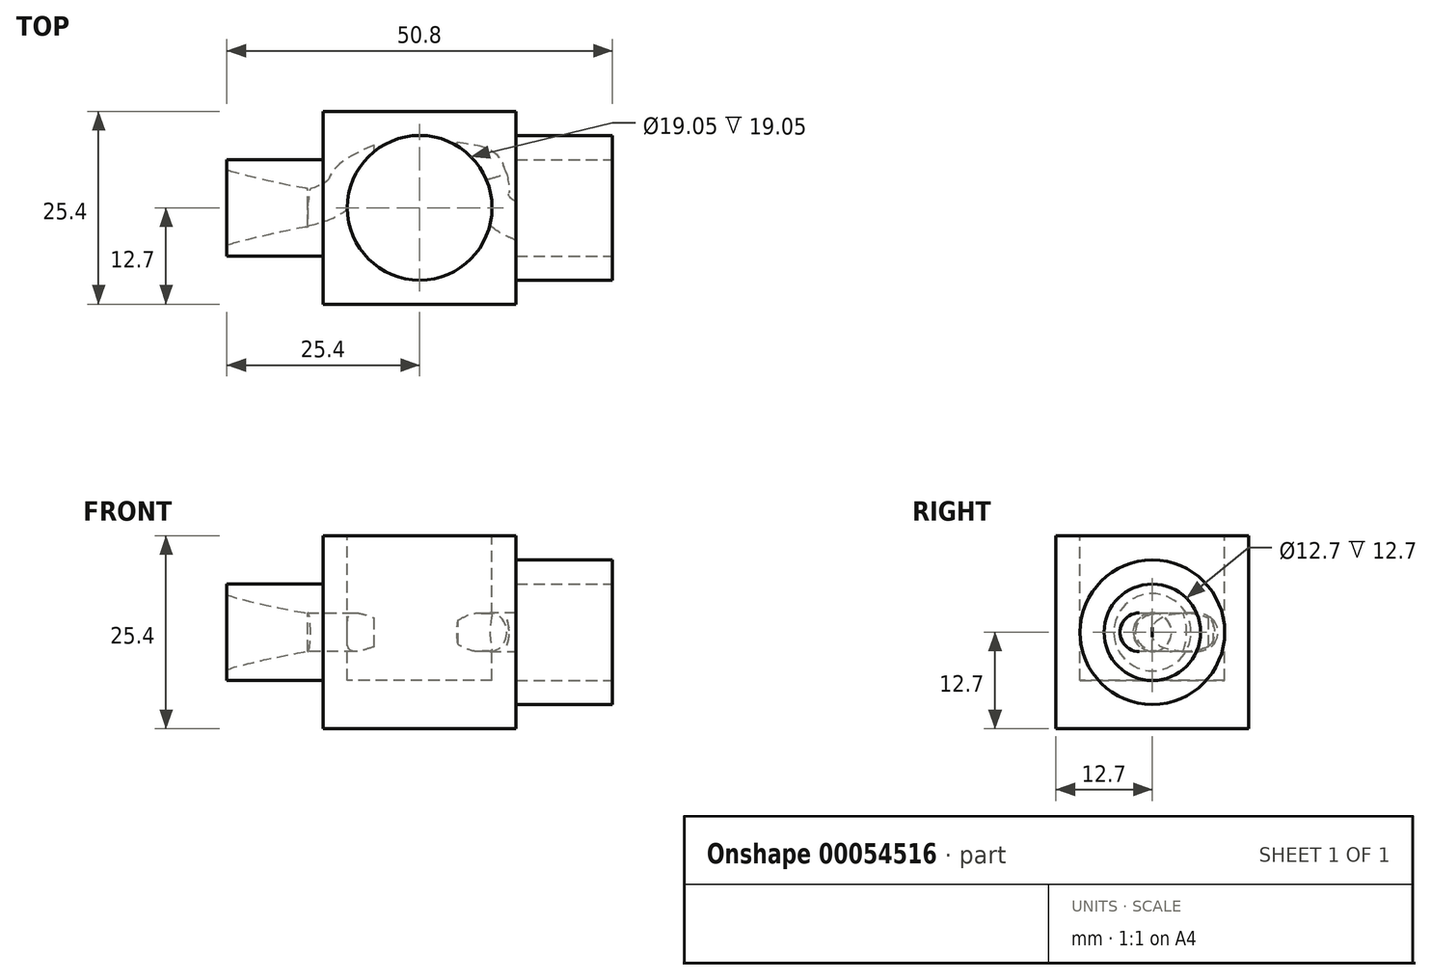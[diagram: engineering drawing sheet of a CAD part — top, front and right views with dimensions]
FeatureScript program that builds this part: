
annotation { "Feature Type Name" : "Feature", "Feature Type Description" : "" }
export const myFeature = defineFeature(function(context is Context, id is Id, definition is map)
    precondition{}
    {
        {
            var Q0;
            Q0=qCreatedBy(makeId("Right.planeOp"),FACE);
            var sketch = newSketch(context, id + "F0", { "sketchPlane" : qUnion([Q0])});
            skCircle(sketch, "E0", {"center": v(0, 0) * mm, "radius": 6.35 * mm});
            skSolve(sketch);
        }
        {
            var Q0;
            Q0=makeQuery(id+"F0.imprint","IMPRINT",FACE,{"disambiguationData":[TD([[makeQuery(id+"F0.imprint","IMPRINT",EDGE,{"derivedFrom":sQuery(id+"F0.wireOp",EDGE,"E0")}),1.0]])]});
            extrude(context, id + "F1", {"entities" : qUnion([Q0]), "depth" : 12.7 * mm});
        }
        {
            var Q0;
            Q0=makeQuery(id+"F1.opExtrude","CAP_FACE",FACE,{"disambiguationData":[OSD([sQuery(id+"F0.wireOp",EDGE,"E0")])],"isStart":false});
            var sketch = newSketch(context, id + "F2", { "sketchPlane" : qUnion([Q0])});
            skLineSegment(sketch, "E1.rect.bottom", {"start": v(12.7, -12.7) * mm, "end": v(-12.7, -12.7) * mm});
            skLineSegment(sketch, "E1.rect.top", {"start": v(12.7, 12.7) * mm, "end": v(-12.7, 12.7) * mm});
            skLineSegment(sketch, "E1.rect.left", {"start": v(12.7, -12.7) * mm, "end": v(12.7, 12.7) * mm});
            skLineSegment(sketch, "E1.rect.right", {"start": v(-12.7, -12.7) * mm, "end": v(-12.7, 12.7) * mm});
            skPoint(sketch, "E1.rect.middle", {"position": v(0, 0) * mm});
            skSolve(sketch);
        }
        {
            var Q0;
            Q0=makeQuery(id+"F2.imprint","IMPRINT",FACE,{"disambiguationData":[TD([[makeQuery(id+"F2.imprint","IMPRINT",EDGE,{"derivedFrom":sQuery(id+"F2.wireOp",EDGE,"E1.rect.bottom")}),-1.0]])]});
            var Q1;
            Q1=makeQuery(id+"F2.imprint","IMPRINT",FACE,{"disambiguationData":[TD([[makeQuery(id+"F2.imprint","IMPRINT",EDGE,{"derivedFrom":makeQuery(id+"F1.opExtrude","CAP_EDGE",EDGE,{"disambiguationData":[OSD([sQuery(id+"F0.wireOp",EDGE,"E0")])],"isStart":false})}),1.0]])]});
            extrude(context, id + "F3", {"entities" : qUnion([Q0, Q1]), "operationType" : NewBodyOperationType.ADD, "depth" : 25.4 * mm});
        }
        {
            var Q0;
            Q0=makeQuery(id+"F3.opExtrude","CAP_FACE",FACE,{"disambiguationData":[OSD([sQuery(id+"F2.wireOp",EDGE,"E1.rect.bottom"),sQuery(id+"F2.wireOp",EDGE,"E1.rect.top"),sQuery(id+"F2.wireOp",EDGE,"E1.rect.left"),sQuery(id+"F2.wireOp",EDGE,"E1.rect.right")])],"isStart":false});
            var sketch = newSketch(context, id + "F4", { "sketchPlane" : qUnion([Q0])});
            skCircle(sketch, "E2", {"center": v(0, 0) * mm, "radius": 9.53 * mm});
            skSolve(sketch);
        }
        {
            var Q0;
            Q0=makeQuery(id+"F4.imprint","IMPRINT",FACE,{"disambiguationData":[TD([[makeQuery(id+"F4.imprint","IMPRINT",EDGE,{"derivedFrom":sQuery(id+"F4.wireOp",EDGE,"E2")}),1.0]])]});
            extrude(context, id + "F5", {"entities" : qUnion([Q0]), "operationType" : NewBodyOperationType.ADD, "depth" : 12.7 * mm});
        }
        {
            var Q0;
            Q0=makeQuery(id+"F3.opExtrude","SWEPT_FACE",FACE,{"disambiguationData":[OSD([sQuery(id+"F2.wireOp",EDGE,"E1.rect.top")])]});
            var sketch = newSketch(context, id + "F6", { "sketchPlane" : qUnion([Q0])});
            skCircle(sketch, "E3", {"center": v(25.4, 0) * mm, "radius": 9.53 * mm});
            skPoint(sketch, "E3.centerSnap0", {"position": v(25.4, 12.7) * mm});
            skSolve(sketch);
        }
        {
            var Q0;
            Q0=makeQuery(id+"F6.imprint","IMPRINT",FACE,{"disambiguationData":[TD([[makeQuery(id+"F6.imprint","IMPRINT",EDGE,{"derivedFrom":sQuery(id+"F6.wireOp",EDGE,"E3")}),1.0]])]});
            extrude(context, id + "F7", {"entities" : qUnion([Q0]), "operationType" : NewBodyOperationType.REMOVE, "oppositeDirection" : true, "depth" : 19.05 * mm});
        }
        {
            var Q0;
            Q0=makeQuery(id+"F5.opExtrude","CAP_FACE",FACE,{"disambiguationData":[OSD([sQuery(id+"F4.wireOp",EDGE,"E2")])],"isStart":false});
            var sketch = newSketch(context, id + "F8", { "sketchPlane" : qUnion([Q0])});
            skCircle(sketch, "E4", {"center": v(0, 0) * mm, "radius": 6.35 * mm});
            skSolve(sketch);
        }
        {
            var Q0;
            Q0=makeQuery(id+"F8.imprint","IMPRINT",FACE,{"disambiguationData":[TD([[makeQuery(id+"F8.imprint","IMPRINT",EDGE,{"derivedFrom":sQuery(id+"F8.wireOp",EDGE,"E4")}),1.0]])]});
            extrude(context, id + "F9", {"entities" : qUnion([Q0]), "operationType" : NewBodyOperationType.REMOVE, "oppositeDirection" : true, "depth" : 12.7 * mm});
        }
        {
            var Q0;
            Q0=qCreatedBy(makeId("Top.planeOp"),FACE);
            var sketch = newSketch(context, id + "F10", { "sketchPlane" : qUnion([Q0])});
            skFitSpline(sketch, "E5", {"points": [v(39.02, -2.8) * mm, v(35.9, -0.94) * mm, v(34.09, 3.67) * mm], "startDerivative": vector(-5.52, 2.94) * mm, "endDerivative": vector(-2.59, 9.24) * mm});
            skFitSpline(sketch, "E6", {"points": [v(34.09, 3.67) * mm, v(33.42, 4.76) * mm, v(31.05, 5.54) * mm], "startDerivative": vector(-1.08, 2.87) * mm, "endDerivative": vector(-4.79, 0.97) * mm});
            skSolve(sketch);
        }
        {
            var Q0;
            Q0=makeQuery(id+"F9.boolean.opBoolean","COPY",FACE,{"derivedFrom":makeQuery(id+"F9.opExtrude","CAP_FACE",FACE,{"disambiguationData":[OSD([sQuery(id+"F8.wireOp",EDGE,"E4")])],"isStart":false})});
            var sketch = newSketch(context, id + "F11", { "sketchPlane" : qUnion([Q0])});
            skCircle(sketch, "E7", {"center": v(-1.73, 0) * mm, "radius": 2.54 * mm});
            skSolve(sketch);
        }
        {
            var Q0;
            Q0=makeQuery(id+"F11.imprint","IMPRINT",FACE,{"disambiguationData":[TD([[makeQuery(id+"F11.imprint","IMPRINT",EDGE,{"derivedFrom":sQuery(id+"F11.wireOp",EDGE,"E7")}),1.0]])]});
            var Q1;
            Q1=sQuery(id+"F10.wireOp",EDGE,"E5");
            var Q2;
            Q2=sQuery(id+"F10.wireOp",EDGE,"E6");
            sweep(context, id + "F12", {"operationType" : NewBodyOperationType.REMOVE, "profiles" : qUnion([Q0]), "path" : qUnion([Q1, Q2])});
        }
        {
            var Q0;
            Q0=qCreatedBy(makeId("Top.planeOp"),FACE);
            var sketch = newSketch(context, id + "F13", { "sketchPlane" : qUnion([Q0])});
            skFitSpline(sketch, "E8", {"points": [v(19.4, 5.72) * mm, v(16.24, 3.85) * mm, v(14.09, 1.48) * mm, v(10.64, 0) * mm], "startDerivative": vector(-10.21, -4.75) * mm, "endDerivative": vector(-11.1, -3.3) * mm});
            skSolve(sketch);
        }
        {
            var Q0;
            Q0=sQuery(id+"F13.wireOp",VERTEX,"E8.start");
            var Q1;
            Q1=qCreatedBy(makeId("Right.planeOp"),FACE);
            cPlane(context, id + "F14", {"entities" : qUnion([Q0, Q1]), "cplaneType" : CPlaneType.PLANE_POINT, "offset" : 152.4 * mm, "width" : 152.4 * mm, "height" : 152.4 * mm});
        }
        {
            var Q0;
            Q0=qCreatedBy(id+"F14.planeOp",FACE);
            var sketch = newSketch(context, id + "F15", { "sketchPlane" : qUnion([Q0])});
            skCircle(sketch, "E9", {"center": v(5.72, 0) * mm, "radius": 2.54 * mm});
            skSolve(sketch);
        }
        {
            var Q0;
            Q0=makeQuery(id+"F15.imprint","IMPRINT",FACE,{"disambiguationData":[TD([[makeQuery(id+"F15.imprint","IMPRINT",EDGE,{"derivedFrom":sQuery(id+"F15.wireOp",EDGE,"E9")}),1.0]])]});
            var Q1;
            Q1=sQuery(id+"F13.wireOp",EDGE,"E8");
            sweep(context, id + "F16", {"operationType" : NewBodyOperationType.REMOVE, "profiles" : qUnion([Q0]), "path" : qUnion([Q1])});
        }
        {
            var Q0;
            Q0=makeQuery(id+"F1.opExtrude","CAP_FACE",FACE,{"disambiguationData":[OSD([sQuery(id+"F0.wireOp",EDGE,"E0")])],"isStart":true});
            var sketch = newSketch(context, id + "F17", { "sketchPlane" : qUnion([Q0])});
            skCircle(sketch, "E10", {"center": v(0, 0) * mm, "radius": 5.08 * mm});
            skSolve(sketch);
        }
        {
            var Q0;
            Q0=sQuery(id+"F13.wireOp",VERTEX,"E8.3.internal");
            var Q1;
            Q1=qCreatedBy(makeId("Right.planeOp"),FACE);
            cPlane(context, id + "F18", {"entities" : qUnion([Q0, Q1]), "cplaneType" : CPlaneType.PLANE_POINT, "offset" : 152.4 * mm, "width" : 152.4 * mm, "height" : 152.4 * mm});
        }
        {
            var Q0;
            Q0=qCreatedBy(id+"F18.planeOp",FACE);
            var sketch = newSketch(context, id + "F19", { "sketchPlane" : qUnion([Q0])});
            skCircle(sketch, "E11", {"center": v(0, 0) * mm, "radius": 2.54 * mm});
            skSolve(sketch);
        }
        {
            var Q1;
            Q1=makeQuery(id+"F17.imprint","IMPRINT",FACE,{"disambiguationData":[TD([[makeQuery(id+"F17.imprint","IMPRINT",EDGE,{"derivedFrom":sQuery(id+"F17.wireOp",EDGE,"E10")}),1.0]])]});
            var Q2;
            Q2 = qSketchRegion(id + "F19", true);
            var Q3;
            Q3=sQuery(id+"F19.wireOp",EDGE,"E11");
            var Q4;
            Q4=sQuery(id+"F17.wireOp",EDGE,"E10");
            loft(context, id + "F20", {"operationType" : NewBodyOperationType.REMOVE, "startCondition" : LoftEndDerivativeType.MATCH_CURVATURE, "startMagnitude" : .3, "endCondition" : LoftEndDerivativeType.NORMAL_TO_PROFILE, "endMagnitude" : .3, "sheetProfilesArray" : [{ "sheetProfileEntities" : qUnion([Q1]) }, { "sheetProfileEntities" : qUnion([Q2]) }], "guidesArray" : [{ "guideEntities" : qUnion([Q3]), "guideDerivativeType" : LoftGuideDerivativeType.DEFAULT, "guideDerivativeMagnitude" : 1 }, { "guideEntities" : qUnion([Q4]), "guideDerivativeType" : LoftGuideDerivativeType.DEFAULT, "guideDerivativeMagnitude" : 1 }]});
        }
    });
